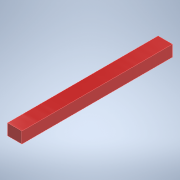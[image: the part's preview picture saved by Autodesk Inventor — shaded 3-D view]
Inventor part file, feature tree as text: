
AUTODESK INVENTOR PART (.ipt)
format: ipt  version: 2021 (Build 250183000, 183)  size: 95,744 bytes
history: native  units: mm
features: other x1, extrude x1, sketch x1
ambient origin geometry x8: Origin, YZ Plane, XZ Plane, XY Plane, X Axis, Y Axis, Z Axis, Center Point
bodies: Body1 (feature_tree)
feature tree (3):
  other  "Sólido1"
  extrude  "Extrusão1"  Depth=15.0mm
  sketch  "Esboço1"  dims[d0=19.0mm d1=15.0mm d2=200.0mm d3=0.0mm]
